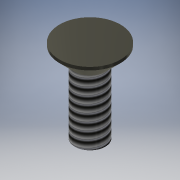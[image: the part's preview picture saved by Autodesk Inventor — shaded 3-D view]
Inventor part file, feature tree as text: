
AUTODESK INVENTOR PART (.ipt)
format: ipt  version: 2016 (Build 200138000, 138)  size: 128,512 bytes
history: native  units: mm
features: extrude x3, sketch x3, other x1, thread x1, chamfer x1
ambient origin geometry x1: Origin
bodies: Body1 (feature_tree)
feature tree (9):
  other  "ソリッド1"
  extrude  "押し出し1"  Depth=2.0mm
  extrude  "押し出し2"  Depth=6.0mm TaperAngle=0.0deg
  thread  "ねじ1"
  chamfer  "面取り1"  Distance=4.0mm
  extrude  "押し出し4"  Depth=1.2mm TaperAngle=0.0deg
  sketch  "スケッチ1"
  sketch  "スケッチ2"
  sketch  "スケッチ4"
